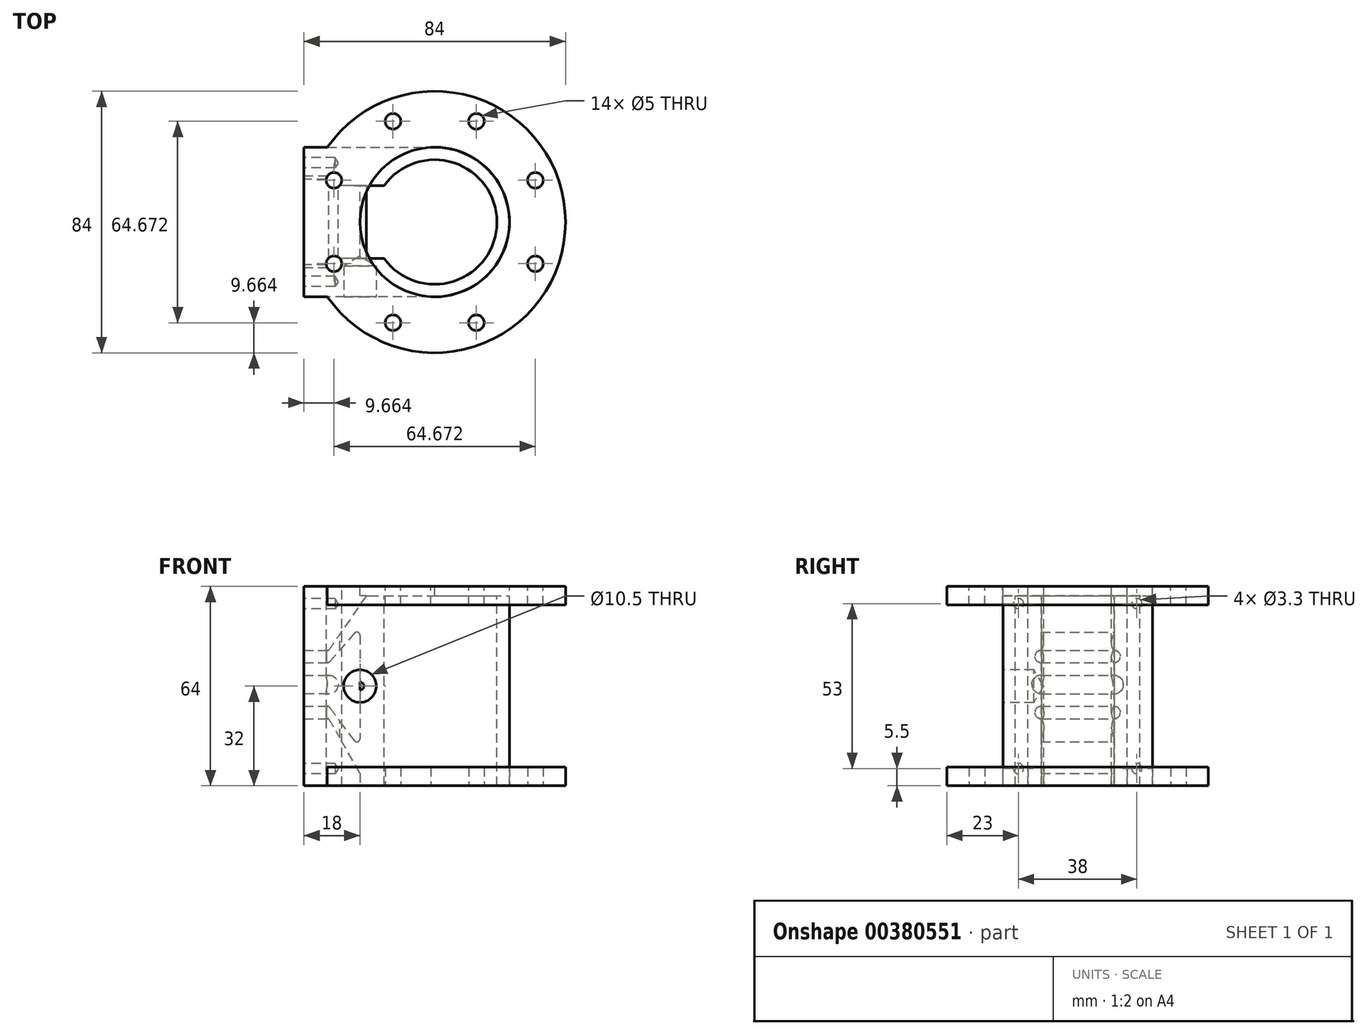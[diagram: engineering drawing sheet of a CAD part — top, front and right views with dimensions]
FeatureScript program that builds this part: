
annotation { "Feature Type Name" : "Feature", "Feature Type Description" : "" }
export const myFeature = defineFeature(function(context is Context, id is Id, definition is map)
    precondition{}
    {
        {
            var Q0;
            Q0=qCreatedBy(makeId("Top.planeOp"),FACE);
            var sketch = newSketch(context, id + "F0", { "sketchPlane" : qUnion([Q0])});
            skArc(sketch, "E0", {"start": v(-34.47, -24) * mm, "mid": v(42, 0) * mm, "end": v(-34.47, 24) * mm});
            skCircle(sketch, "E1", {"center": v(0, 0) * mm, "radius": 20 * mm});
            skCircle(sketch, "E2", {"center": v(0, 0) * mm, "radius": 35 * mm, "construction": true});
            skLineSegment(sketch, "E3", {"start": v(0, 71.76) * mm, "end": v(0, 20) * mm, "construction": true});
            skLineSegment(sketch, "E4", {"start": v(-64.72, 0) * mm, "end": v(-10.92, 0) * mm, "construction": true});
            skLineSegment(sketch, "E5", {"start": v(-12.55, 5.2) * mm, "end": v(-110.75, 45.87) * mm, "construction": true});
            skLineSegment(sketch, "E6", {"start": v(-7.65, 18.48) * mm, "end": v(-42.73, 103.16) * mm, "construction": true});
            skCircle(sketch, "E7", {"center": v(-32.34, 13.4) * mm, "radius": 2.5 * mm});
            skCircle(sketch, "E8", {"center": v(-13.4, 32.34) * mm, "radius": 2.5 * mm});
            skCircle(sketch, "E9.MirrorC", {"center": v(13.4, 32.34) * mm, "radius": 2.5 * mm});
            skCircle(sketch, "E10.MirrorC", {"center": v(32.34, 13.4) * mm, "radius": 2.5 * mm});
            skCircle(sketch, "E11.MirrorC", {"center": v(32.34, -13.4) * mm, "radius": 2.5 * mm});
            skCircle(sketch, "E12.MirrorC", {"center": v(13.4, -32.34) * mm, "radius": 2.5 * mm});
            skCircle(sketch, "E13.MirrorC", {"center": v(-13.4, -32.34) * mm, "radius": 2.5 * mm});
            skCircle(sketch, "E14.MirrorC", {"center": v(-32.34, -13.4) * mm, "radius": 2.5 * mm});
            skCircle(sketch, "E15", {"center": v(0, 0) * mm, "radius": 24 * mm});
            skLineSegment(sketch, "E16", {"start": v(0, 24) * mm, "end": v(-42, 24) * mm});
            skLineSegment(sketch, "E17", {"start": v(0, 24) * mm, "end": v(0, -24) * mm, "construction": true});
            skLineSegment(sketch, "E18", {"start": v(0, -24) * mm, "end": v(-42, -24) * mm});
            skLineSegment(sketch, "E19", {"start": v(-42, -24) * mm, "end": v(-42, 24) * mm});
            skLineSegment(sketch, "E20", {"start": v(-19.69, 3.53) * mm, "end": v(-38.39, 3.53) * mm, "construction": true});
            skLineSegment(sketch, "E21", {"start": v(-38.39, 3.53) * mm, "end": v(-38.39, -3.53) * mm, "construction": true});
            skLineSegment(sketch, "E22", {"start": v(-38.39, -3.53) * mm, "end": v(-19.69, -3.53) * mm, "construction": true});
            skPoint(sketch, "E23", {"position": v(-38.39, 0) * mm});
            skCircle(sketch, "E24", {"center": v(-20, 0) * mm, "radius": 9.08 * mm, "construction": true});
            skLineSegment(sketch, "E25.bottom", {"start": v(-42, -21) * mm, "end": v(-32.3, -21) * mm, "construction": true});
            skLineSegment(sketch, "E25.top", {"start": v(-42, -17.1) * mm, "end": v(-32.3, -17.1) * mm, "construction": true});
            skLineSegment(sketch, "E25.left", {"start": v(-42, -21) * mm, "end": v(-42, -17.1) * mm, "construction": true});
            skLineSegment(sketch, "E25.right", {"start": v(-32.3, -21) * mm, "end": v(-32.3, -17.1) * mm, "construction": true});
            skLineSegment(sketch, "E26.bottom", {"start": v(-42, 21.16) * mm, "end": v(-32.38, 21.16) * mm, "construction": true});
            skLineSegment(sketch, "E26.top", {"start": v(-42, 17.49) * mm, "end": v(-32.38, 17.49) * mm, "construction": true});
            skLineSegment(sketch, "E26.left", {"start": v(-42, 21.16) * mm, "end": v(-42, 17.49) * mm});
            skLineSegment(sketch, "E26.right", {"start": v(-32.38, 21.16) * mm, "end": v(-32.38, 17.49) * mm, "construction": true});
            skLineSegment(sketch, "E27.bottom", {"start": v(-34.59, 9.94) * mm, "end": v(-30.32, 9.94) * mm, "construction": true});
            skLineSegment(sketch, "E27.top", {"start": v(-34.59, -9.9) * mm, "end": v(-30.32, -9.9) * mm, "construction": true});
            skLineSegment(sketch, "E27.left", {"start": v(-34.59, 9.94) * mm, "end": v(-34.59, -9.9) * mm, "construction": true});
            skLineSegment(sketch, "E27.right", {"start": v(-30.32, 9.94) * mm, "end": v(-30.32, -9.9) * mm, "construction": true});
            skLineSegment(sketch, "E28.trimOffspring", {"start": v(0, 0) * mm, "end": v(0, -71.76) * mm, "construction": true});
            skLineSegment(sketch, "E29.trimOffspring", {"start": v(20, 0) * mm, "end": v(64.72, 0) * mm, "construction": true});
            skSolve(sketch);
        }
        {
            var Q0;
            Q0=qCreatedBy(makeId("Front.planeOp"),FACE);
            var sketch = newSketch(context, id + "F1", { "sketchPlane" : qUnion([Q0])});
            skLineSegment(sketch, "E30.bottom", {"start": v(-42, 0) * mm, "end": v(42, 0) * mm, "construction": true});
            skLineSegment(sketch, "E30.top", {"start": v(-42, -64) * mm, "end": v(42, -64) * mm, "construction": true});
            skLineSegment(sketch, "E30.left", {"start": v(-42, 0) * mm, "end": v(-42, -64) * mm, "construction": true});
            skLineSegment(sketch, "E30.right", {"start": v(42, 0) * mm, "end": v(42, -64) * mm, "construction": true});
            skLineSegment(sketch, "E31.bottom", {"start": v(-42, 0) * mm, "end": v(42, 0) * mm});
            skLineSegment(sketch, "E31.top", {"start": v(-42, -6) * mm, "end": v(42, -6) * mm});
            skLineSegment(sketch, "E31.left", {"start": v(-42, 0) * mm, "end": v(-42, -6) * mm});
            skLineSegment(sketch, "E31.right", {"start": v(42, 0) * mm, "end": v(42, -6) * mm});
            skLineSegment(sketch, "E32.bottom", {"start": v(-42, -58) * mm, "end": v(42, -58) * mm});
            skLineSegment(sketch, "E32.top", {"start": v(-42, -64) * mm, "end": v(42, -64) * mm});
            skLineSegment(sketch, "E32.left", {"start": v(-42, -58) * mm, "end": v(-42, -64) * mm});
            skLineSegment(sketch, "E32.right", {"start": v(42, -58) * mm, "end": v(42, -64) * mm});
            skLineSegment(sketch, "E33", {"start": v(-24, 0) * mm, "end": v(24, 0) * mm});
            skLineSegment(sketch, "E34", {"start": v(-24, 0) * mm, "end": v(-24, -64) * mm, "construction": true});
            skLineSegment(sketch, "E35", {"start": v(24, 0) * mm, "end": v(24, -64) * mm, "construction": true});
            skLineSegment(sketch, "E36", {"start": v(-20, 0) * mm, "end": v(-20, -64) * mm, "construction": true});
            skLineSegment(sketch, "E37", {"start": v(20.03, 0) * mm, "end": v(20.03, -58) * mm, "construction": true});
            skSolve(sketch);
        }
        {
            var Q0;
            Q0=makeQuery(id+"F0.imprint","IMPRINT",FACE,{"disambiguationData":[TD([[makeQuery(id+"F0.imprint","IMPRINT",EDGE,{"derivedFrom":sQuery(id+"F0.wireOp",EDGE,"E1")}),-1.0]])]});
            var Q1;
            Q1=makeQuery(id+"F0.imprint","IMPRINT",FACE,{"disambiguationData":[TD([[makeQuery(id+"F0.imprint","IMPRINT",EDGE,{"derivedFrom":sQuery(id+"F0.wireOp",EDGE,"E7")}),-1.0]])]});
            extrude(context, id + "F2", {"entities" : qUnion([Q0, Q1]), "oppositeDirection" : true, "depth" : 64 * mm});
        }
        {
            var Q0;
            Q0=qCreatedBy(makeId("Top.planeOp"),FACE);
            var sketch = newSketch(context, id + "F3", { "sketchPlane" : qUnion([Q0])});
            skArc(sketch, "E38", {"start": v(-34.47, -24) * mm, "mid": v(42, 0) * mm, "end": v(-34.47, 24) * mm});
            skLineSegment(sketch, "E39", {"start": v(-20, 0) * mm, "end": v(-20, 0) * mm});
            skLineSegment(sketch, "E40", {"start": v(-142.95, 0) * mm, "end": v(-116.62, 0) * mm, "construction": true});
            skCircle(sketch, "E41", {"center": v(-32.34, 13.4) * mm, "radius": 2.5 * mm});
            skCircle(sketch, "E42", {"center": v(-13.4, 32.34) * mm, "radius": 2.5 * mm});
            skCircle(sketch, "E43.MirrorC", {"center": v(13.4, 32.34) * mm, "radius": 2.5 * mm});
            skCircle(sketch, "E44.MirrorC", {"center": v(32.34, 13.4) * mm, "radius": 2.5 * mm});
            skCircle(sketch, "E45.MirrorC", {"center": v(32.34, -13.4) * mm, "radius": 2.5 * mm});
            skCircle(sketch, "E46.MirrorC", {"center": v(13.4, -32.34) * mm, "radius": 2.5 * mm});
            skCircle(sketch, "E47.MirrorC", {"center": v(-13.4, -32.34) * mm, "radius": 2.5 * mm});
            skCircle(sketch, "E48.MirrorC", {"center": v(-32.34, -13.4) * mm, "radius": 2.5 * mm});
            skLineSegment(sketch, "E49", {"start": v(0, 24) * mm, "end": v(0, 24) * mm});
            skLineSegment(sketch, "E50", {"start": v(-34.47, -24) * mm, "end": v(-42, -24) * mm});
            skLineSegment(sketch, "E51", {"start": v(-42, -24) * mm, "end": v(-42, 24) * mm});
            skLineSegment(sketch, "E52", {"start": v(-116.62, 3.53) * mm, "end": v(-116.62, -3.53) * mm, "construction": true});
            skPoint(sketch, "E53", {"position": v(-116.62, 0) * mm});
            skLineSegment(sketch, "E54.left", {"start": v(-42, -2.64) * mm, "end": v(-42, 1.25) * mm, "construction": true});
            skLineSegment(sketch, "E55.bottom", {"start": v(-112.82, 28.3) * mm, "end": v(-108.56, 28.3) * mm, "construction": true});
            skLineSegment(sketch, "E55.top", {"start": v(-112.82, 8.44) * mm, "end": v(-108.56, 8.44) * mm, "construction": true});
            skLineSegment(sketch, "E55.left", {"start": v(-112.82, 28.3) * mm, "end": v(-112.82, 8.44) * mm, "construction": true});
            skLineSegment(sketch, "E55.right", {"start": v(-108.56, 28.3) * mm, "end": v(-108.56, 8.44) * mm, "construction": true});
            skPoint(sketch, "E56.orphan", {"position": v(0, 53.4) * mm});
            skLineSegment(sketch, "E57.trimOffspring", {"start": v(0, -42) * mm, "end": v(0, -53.4) * mm, "construction": true});
            skLineSegment(sketch, "E58.trimOffspring", {"start": v(-34.47, 24) * mm, "end": v(-42, 24) * mm});
            skPoint(sketch, "E59.trimOffspring.end.orphan", {"position": v(142.95, 0) * mm});
            skCircle(sketch, "E60", {"center": v(0, 0) * mm, "radius": 24.03 * mm});
            skSolve(sketch);
        }
        {
            var Q0;
            Q0=makeQuery(id+"F3.imprint","IMPRINT",FACE,{"disambiguationData":[TD([[makeQuery(id+"F3.imprint","IMPRINT",EDGE,{"derivedFrom":sQuery(id+"F3.wireOp",EDGE,"E38")}),1.0]])]});
            extrude(context, id + "F4", {"entities" : qUnion([Q0]), "operationType" : NewBodyOperationType.ADD, "oppositeDirection" : true, "depth" : 6 * mm});
        }
        {
            var Q0;
            Q0=makeQuery(id+"F2.opExtrude","CAP_FACE",FACE,{"disambiguationData":[OSD([sQuery(id+"F0.wireOp",EDGE,"E1"),sQuery(id+"F0.wireOp",EDGE,"E15")])],"isStart":false});
            var sketch = newSketch(context, id + "F5", { "sketchPlane" : qUnion([Q0])});
            skArc(sketch, "E61.0", {"start": v(0, 24) * mm, "mid": v(24, 0) * mm, "end": v(0, -24) * mm});
            skLineSegment(sketch, "E61.1.0", {"start": v(-1.29, -24) * mm, "end": v(-34.47, -24) * mm});
            skArc(sketch, "E61.1.1", {"start": v(-34.47, -24) * mm, "mid": v(42, 0) * mm, "end": v(-34.47, 24) * mm});
            skLineSegment(sketch, "E61.1.2", {"start": v(-34.47, 24) * mm, "end": v(-1.29, 24) * mm});
            skArc(sketch, "E61.1.3", {"start": v(-1.29, 24) * mm, "mid": v(24.03, 0) * mm, "end": v(-1.29, -24) * mm});
            skCircle(sketch, "E62.0", {"center": v(13.4, 32.34) * mm, "radius": 2.5 * mm});
            skCircle(sketch, "E62.1", {"center": v(-13.4, 32.34) * mm, "radius": 2.5 * mm});
            skCircle(sketch, "E62.3", {"center": v(32.34, 13.4) * mm, "radius": 2.5 * mm});
            skCircle(sketch, "E62.4", {"center": v(32.34, -13.4) * mm, "radius": 2.5 * mm});
            skCircle(sketch, "E62.5", {"center": v(13.4, -32.34) * mm, "radius": 2.5 * mm});
            skCircle(sketch, "E62.7", {"center": v(-13.4, -32.34) * mm, "radius": 2.5 * mm});
            skSolve(sketch);
        }
        {
            var Q0;
            Q0=makeQuery(id+"F5.imprint","IMPRINT",FACE,{"disambiguationData":[TD([[makeQuery(id+"F5.imprint","IMPRINT",EDGE,{"derivedFrom":sQuery(id+"F5.wireOp",EDGE,"E61.1.0")}),1.0]])]});
            extrude(context, id + "F6", {"entities" : qUnion([Q0]), "operationType" : NewBodyOperationType.ADD, "oppositeDirection" : true, "depth" : 6 * mm});
        }
        {
            var Q0;
            Q0=makeQuery(id+"F2.opExtrude","SWEPT_FACE",FACE,{"disambiguationData":[OSD([sQuery(id+"F0.wireOp",EDGE,"E18")])]});
            var sketch = newSketch(context, id + "F7", { "sketchPlane" : qUnion([Q0])});
            skPoint(sketch, "E63.0", {"position": v(-24, -32) * mm});
            skSolve(sketch);
        }
        {
            var Q0;
            Q0=makeQuery(id+"F2.opExtrude","SWEPT_FACE",FACE,{"disambiguationData":[OSD([sQuery(id+"F0.wireOp",EDGE,"E19"),sQuery(id+"F0.wireOp",EDGE,"E26.left")])]});
            var sketch = newSketch(context, id + "F8", { "sketchPlane" : qUnion([Q0])});
            skCircle(sketch, "E64", {"center": v(-19, -5.5) * mm, "radius": 2.65 * mm});
            skCircle(sketch, "E65.MirrorC", {"center": v(19, -5.5) * mm, "radius": 2.65 * mm});
            skLineSegment(sketch, "E66", {"start": v(0, 0) * mm, "end": v(0, -64) * mm, "construction": true});
            skLineSegment(sketch, "E67", {"start": v(60.89, -32) * mm, "end": v(-49.42, -32) * mm, "construction": true});
            skPoint(sketch, "E67.startSnap0", {"position": v(0, -32) * mm});
            skCircle(sketch, "E68.MirrorC", {"center": v(-19, -58.5) * mm, "radius": 2.65 * mm});
            skCircle(sketch, "E69.MirrorC", {"center": v(19, -58.5) * mm, "radius": 2.65 * mm});
            skSolve(sketch);
        }
        {
            var Q0;
            Q0=sQuery(id+"F8.wireOp",VERTEX,"E64.center");
            var Q1;
            Q1=sQuery(id+"F8.wireOp",VERTEX,"E65.MirrorC.center");
            var Q2;
            Q2=sQuery(id+"F8.wireOp",VERTEX,"E68.MirrorC.center");
            var Q3;
            Q3=sQuery(id+"F8.wireOp",VERTEX,"E69.MirrorC.center");
            var Q4;
            Q4=makeQuery(id+"F2.opExtrude","SWEPT_BODY",BODY,{"disambiguationData":[OSD([sQuery(id+"F0.wireOp",EDGE,"E1"),sQuery(id+"F0.wireOp",EDGE,"E7"),sQuery(id+"F0.wireOp",EDGE,"E14.MirrorC"),sQuery(id+"F0.wireOp",EDGE,"E15"),sQuery(id+"F0.wireOp",EDGE,"E16"),sQuery(id+"F0.wireOp",EDGE,"E18"),sQuery(id+"F0.wireOp",EDGE,"E19"),sQuery(id+"F0.wireOp",EDGE,"E26.left")])]});
            hole(context, id + "F9", {"style" : HoleStyle.SIMPLE, "endStyle" : HoleEndStyle.BLIND, "holeDiameter" : 3.3 * mm, "holeDepth" : 10 * mm, "tappedDepth" : 12.7 * mm, "tapClearance" : 3, "locations" : qUnion([Q0, Q1, Q2, Q3]), "scope" : qUnion([Q4])});
        }
        {
            var Q0;
            Q0=makeQuery(id+"F0.imprint","IMPRINT",FACE,{"disambiguationData":[TD([[makeQuery(id+"F0.imprint","IMPRINT",EDGE,{"derivedFrom":sQuery(id+"F0.wireOp",EDGE,"E1")}),-1.0]])]});
            extrude(context, id + "F10", {"entities" : qUnion([Q0]), "operationType" : NewBodyOperationType.REMOVE, "oppositeDirection" : true, "depth" : 3 * mm});
        }
        {
            var Q0;
            Q0=qCreatedBy(makeId("Front.planeOp"),FACE);
            cPlane(context, id + "F11", {"entities" : qUnion([Q0]), "cplaneType" : CPlaneType.OFFSET, "offset" : 55.7 * mm, "oppositeDirection" : true, "width" : 150 * mm, "height" : 150 * mm});
        }
        {
            var Q0;
            Q0=qCreatedBy(id+"F11.planeOp",FACE);
            var sketch = newSketch(context, id + "F12", { "sketchPlane" : qUnion([Q0])});
            skLineSegment(sketch, "E70.bottom", {"start": v(-63.22, 16.05) * mm, "end": v(57.63, 16.05) * mm});
            skLineSegment(sketch, "E70.top", {"start": v(-63.22, -69.82) * mm, "end": v(57.63, -69.82) * mm});
            skLineSegment(sketch, "E70.left", {"start": v(-63.22, 16.05) * mm, "end": v(-63.22, -69.82) * mm});
            skLineSegment(sketch, "E70.right", {"start": v(57.63, 16.05) * mm, "end": v(57.63, -69.82) * mm});
            skSolve(sketch);
        }
        {
            var Q0;
            Q0=makeQuery(id+"F12.imprint","IMPRINT",FACE,{"disambiguationData":[TD([[makeQuery(id+"F12.imprint","IMPRINT",EDGE,{"derivedFrom":sQuery(id+"F12.wireOp",EDGE,"E70.bottom")}),-1.0]])]});
            extrude(context, id + "F13", {"entities" : qUnion([Q0]), "operationType" : NewBodyOperationType.REMOVE, "depth" : 55.4 * mm});
        }
        {
            var Q0;
            {var subQ4=sQuery(id+"F0.wireOp",EDGE,"E15");Q0=makeQuery(id+"F13.boolean.opBoolean","COPY",FACE,{"disambiguationData":[TD([makeQuery(id+"F10.boolean.opBoolean","COPY",FACE,{"derivedFrom":makeQuery(id+"F10.opExtrude","SWEPT_FACE",FACE,{"disambiguationData":[OSD([subQ4])]})})])],"derivedFrom":makeQuery(id+"F13.opExtrude","CAP_FACE",FACE,{"disambiguationData":[OSD([sQuery(id+"F12.wireOp",EDGE,"E70.bottom"),sQuery(id+"F12.wireOp",EDGE,"E70.top"),sQuery(id+"F12.wireOp",EDGE,"E70.left"),sQuery(id+"F12.wireOp",EDGE,"E70.right")])],"isStart":false})});}
            var sketch = newSketch(context, id + "F14", { "sketchPlane" : qUnion([Q0])});
            skLineSegment(sketch, "E71", {"start": v(24, -15.66) * mm, "end": v(24, -48.92) * mm});
            skLineSegment(sketch, "E72", {"start": v(42, -28.5) * mm, "end": v(34, -28.5) * mm});
            skLineSegment(sketch, "E73", {"start": v(34, -28.5) * mm, "end": v(34, -34.5) * mm, "construction": true});
            skLineSegment(sketch, "E74", {"start": v(34, -34.5) * mm, "end": v(42, -34.5) * mm});
            skLineSegment(sketch, "E75", {"start": v(24, -60) * mm, "end": v(24, -64) * mm});
            skArc(sketch, "E76", {"start": v(34, -28.5) * mm, "mid": v(31, -31.5) * mm, "end": v(34, -34.5) * mm});
            skLineSegment(sketch, "E77.bottom", {"start": v(42, -20.5) * mm, "end": v(34, -20.5) * mm});
            skLineSegment(sketch, "E77.top", {"start": v(42, -24.5) * mm, "end": v(34.46, -24.5) * mm});
            skLineSegment(sketch, "E77.left", {"start": v(42, -20.5) * mm, "end": v(42, -24.5) * mm});
            skLineSegment(sketch, "E77.right", {"start": v(34, -20.5) * mm, "end": v(34, -24.5) * mm, "construction": true});
            skLineSegment(sketch, "E78.bottom", {"start": v(42, -38.5) * mm, "end": v(34.5, -38.5) * mm});
            skLineSegment(sketch, "E78.top", {"start": v(42, -42.5) * mm, "end": v(34, -42.5) * mm});
            skLineSegment(sketch, "E78.left", {"start": v(42, -38.5) * mm, "end": v(42, -42.5) * mm});
            skLineSegment(sketch, "E78.right", {"start": v(34, -38.5) * mm, "end": v(34, -42.5) * mm, "construction": true});
            skLineSegment(sketch, "E79", {"start": v(22, -3) * mm, "end": v(34, -20.5) * mm});
            skLineSegment(sketch, "E80", {"start": v(24, -60) * mm, "end": v(34, -42.5) * mm});
            skLineSegment(sketch, "E81", {"start": v(25.75, -15) * mm, "end": v(33.7, -24.16) * mm});
            skLineSegment(sketch, "E82", {"start": v(25.8, -49.52) * mm, "end": v(33.7, -38.9) * mm});
            skPoint(sketch, "E83.visualSharp", {"position": v(24, -12.99) * mm});
            skArc(sketch, "E83.filletArc", {"start": v(25.75, -15) * mm, "mid": v(24.65, -14.73) * mm, "end": v(24, -15.66) * mm});
            skPoint(sketch, "E84.visualSharp", {"position": v(24, -51.94) * mm});
            skArc(sketch, "E84.filletArc", {"start": v(24, -48.92) * mm, "mid": v(24.68, -49.87) * mm, "end": v(25.8, -49.52) * mm});
            skPoint(sketch, "E85.visualSharp", {"position": v(34, -24.5) * mm});
            skArc(sketch, "E85.filletArc", {"start": v(33.7, -24.16) * mm, "mid": v(34.04, -24.4) * mm, "end": v(34.46, -24.5) * mm});
            skPoint(sketch, "E86.visualSharp", {"position": v(34, -38.5) * mm});
            skArc(sketch, "E86.filletArc", {"start": v(34.5, -38.5) * mm, "mid": v(34.05, -38.6) * mm, "end": v(33.7, -38.9) * mm});
            skLineSegment(sketch, "E87", {"start": v(22, -3) * mm, "end": v(20, -3) * mm});
            skLineSegment(sketch, "E88", {"start": v(20, -64) * mm, "end": v(24, -64) * mm});
            skLineSegment(sketch, "E89", {"start": v(42, -42.5) * mm, "end": v(42, -20.5) * mm});
            skLineSegment(sketch, "E90", {"start": v(16.24, -3) * mm, "end": v(16.24, -64) * mm});
            skLineSegment(sketch, "E91", {"start": v(16.24, -3) * mm, "end": v(20, -3) * mm});
            skLineSegment(sketch, "E92", {"start": v(16.24, -64) * mm, "end": v(20, -64) * mm});
            skSolve(sketch);
        }
        {
            var Q0;
            Q0=makeQuery(id+"F14.imprint","IMPRINT",FACE,{"disambiguationData":[TD([[makeQuery(id+"F14.imprint","IMPRINT",EDGE,{"derivedFrom":sQuery(id+"F14.wireOp",EDGE,"E71")}),-1.0]])]});
            var Q1;
            {var subQ0=sQuery(id+"F14.wireOp",EDGE,"E72");Q1=makeQuery(id+"F14.imprint","IMPRINT",FACE,{"disambiguationData":[TD([[makeQuery(id+"F14.imprint","IMPRINT",EDGE,{"derivedFrom":subQ0}),1.0]])]});}
            var Q2;
            Q2=makeQuery(id+"F14.imprint","IMPRINT",FACE,{"disambiguationData":[TD([[makeQuery(id+"F14.imprint","IMPRINT",EDGE,{"derivedFrom":sQuery(id+"F14.wireOp",EDGE,"E90")}),1.0]])]});
            extrude(context, id + "F15", {"entities" : qUnion([Q0, Q1, Q2]), "operationType" : NewBodyOperationType.REMOVE, "oppositeDirection" : true, "depth" : 12 * mm});
        }
        {
            var Q0;
            Q0=makeQuery(id+"F2.opExtrude","SWEPT_BODY",BODY,{"disambiguationData":[OSD([sQuery(id+"F0.wireOp",EDGE,"E1"),sQuery(id+"F0.wireOp",EDGE,"E7"),sQuery(id+"F0.wireOp",EDGE,"E14.MirrorC"),sQuery(id+"F0.wireOp",EDGE,"E15"),sQuery(id+"F0.wireOp",EDGE,"E16"),sQuery(id+"F0.wireOp",EDGE,"E18"),sQuery(id+"F0.wireOp",EDGE,"E19"),sQuery(id+"F0.wireOp",EDGE,"E26.left")])]});
            var Q1;
            Q1=qCreatedBy(makeId("Front.planeOp"),FACE);
            mirror(context, id + "F16", {"operationType" : NewBodyOperationType.ADD, "entities" : qUnion([Q0]), "mirrorPlane" : qUnion([Q1])});
        }
        {
            var Q0;
            Q0=sQuery(id+"F7.wireOp",VERTEX,"E63.0");
            var Q1;
            Q1=makeQuery(id+"F2.opExtrude","SWEPT_BODY",BODY,{"disambiguationData":[OSD([sQuery(id+"F0.wireOp",EDGE,"E1"),sQuery(id+"F0.wireOp",EDGE,"E7"),sQuery(id+"F0.wireOp",EDGE,"E14.MirrorC"),sQuery(id+"F0.wireOp",EDGE,"E15"),sQuery(id+"F0.wireOp",EDGE,"E16"),sQuery(id+"F0.wireOp",EDGE,"E18"),sQuery(id+"F0.wireOp",EDGE,"E19"),sQuery(id+"F0.wireOp",EDGE,"E26.left")])]});
            hole(context, id + "F17", {"style" : HoleStyle.SIMPLE, "endStyle" : HoleEndStyle.BLIND, "holeDiameter" : 10.5 * mm, "holeDepth" : 9.9 * mm, "tappedDepth" : 12.7 * mm, "tapClearance" : 3, "locations" : qUnion([Q0]), "scope" : qUnion([Q1])});
        }
        {
            var Q0;
            {var subQ0=makeQuery(id+"F2.opExtrude","SWEPT_FACE",FACE,{"disambiguationData":[OSD([sQuery(id+"F0.wireOp",EDGE,"E19"),sQuery(id+"F0.wireOp",EDGE,"E26.left")])]});Q0=makeQuery(id+"F16.boolean.opBoolean","MERGE",FACE,{"derivedFrom":[subQ0,makeQuery(id+"F16.opPattern","COPY",FACE,{"derivedFrom":subQ0,"instanceName":"1"})]});}
            var sketch = newSketch(context, id + "F18", { "sketchPlane" : qUnion([Q0])});
            skArc(sketch, "E93", {"start": v(-11.7, -20.5) * mm, "mid": v(-13.7, -22.5) * mm, "end": v(-11.7, -24.5) * mm});
            skArc(sketch, "E94", {"start": v(11.7, -24.5) * mm, "mid": v(13.7, -22.5) * mm, "end": v(11.7, -20.5) * mm});
            skArc(sketch, "E95", {"start": v(11.7, -34.5) * mm, "mid": v(14.7, -31.5) * mm, "end": v(11.7, -28.5) * mm});
            skArc(sketch, "E96", {"start": v(-11.7, -28.5) * mm, "mid": v(-14.7, -31.5) * mm, "end": v(-11.7, -34.5) * mm});
            skArc(sketch, "E97", {"start": v(-11.7, -38.5) * mm, "mid": v(-13.7, -40.5) * mm, "end": v(-11.7, -42.5) * mm});
            skArc(sketch, "E98", {"start": v(11.7, -42.5) * mm, "mid": v(13.7, -40.5) * mm, "end": v(11.7, -38.5) * mm});
            skLineSegment(sketch, "E99", {"start": v(-11.7, -28.5) * mm, "end": v(11.7, -28.5) * mm});
            skLineSegment(sketch, "E100", {"start": v(11.7, -34.5) * mm, "end": v(-11.7, -34.5) * mm});
            skLineSegment(sketch, "E101", {"start": v(-11.7, -38.5) * mm, "end": v(11.7, -38.5) * mm});
            skLineSegment(sketch, "E102", {"start": v(11.7, -42.5) * mm, "end": v(-11.7, -42.5) * mm});
            skLineSegment(sketch, "E103", {"start": v(-11.7, -34.5) * mm, "end": v(11.7, -34.5) * mm});
            skLineSegment(sketch, "E104", {"start": v(-11.7, -24.5) * mm, "end": v(11.7, -24.5) * mm});
            skLineSegment(sketch, "E105", {"start": v(-11.7, -20.5) * mm, "end": v(11.7, -20.5) * mm});
            skSolve(sketch);
        }
        {
            var Q0;
            Q0=makeQuery(id+"F18.imprint","IMPRINT",FACE,{"disambiguationData":[TD([[makeQuery(id+"F18.imprint","IMPRINT",EDGE,{"derivedFrom":sQuery(id+"F18.wireOp",EDGE,"E93")}),1.0]])]});
            var Q1;
            Q1=makeQuery(id+"F18.imprint","IMPRINT",FACE,{"disambiguationData":[TD([[makeQuery(id+"F18.imprint","IMPRINT",EDGE,{"derivedFrom":sQuery(id+"F18.wireOp",EDGE,"E94")}),1.0]])]});
            var Q2;
            Q2=makeQuery(id+"F18.imprint","IMPRINT",FACE,{"disambiguationData":[TD([[makeQuery(id+"F18.imprint","IMPRINT",EDGE,{"derivedFrom":sQuery(id+"F18.wireOp",EDGE,"E96")}),1.0]])]});
            var Q3;
            Q3=makeQuery(id+"F18.imprint","IMPRINT",FACE,{"disambiguationData":[TD([[makeQuery(id+"F18.imprint","IMPRINT",EDGE,{"derivedFrom":sQuery(id+"F18.wireOp",EDGE,"E95")}),1.0]])]});
            var Q4;
            Q4=makeQuery(id+"F18.imprint","IMPRINT",FACE,{"disambiguationData":[TD([[makeQuery(id+"F18.imprint","IMPRINT",EDGE,{"derivedFrom":sQuery(id+"F18.wireOp",EDGE,"E97")}),1.0]])]});
            var Q5;
            Q5=makeQuery(id+"F18.imprint","IMPRINT",FACE,{"disambiguationData":[TD([[makeQuery(id+"F18.imprint","IMPRINT",EDGE,{"derivedFrom":sQuery(id+"F18.wireOp",EDGE,"E98")}),1.0]])]});
            extrude(context, id + "F19", {"entities" : qUnion([Q0, Q1, Q2, Q3, Q4, Q5]), "operationType" : NewBodyOperationType.REMOVE, "oppositeDirection" : true, "depth" : 10 * mm});
        }
    });
